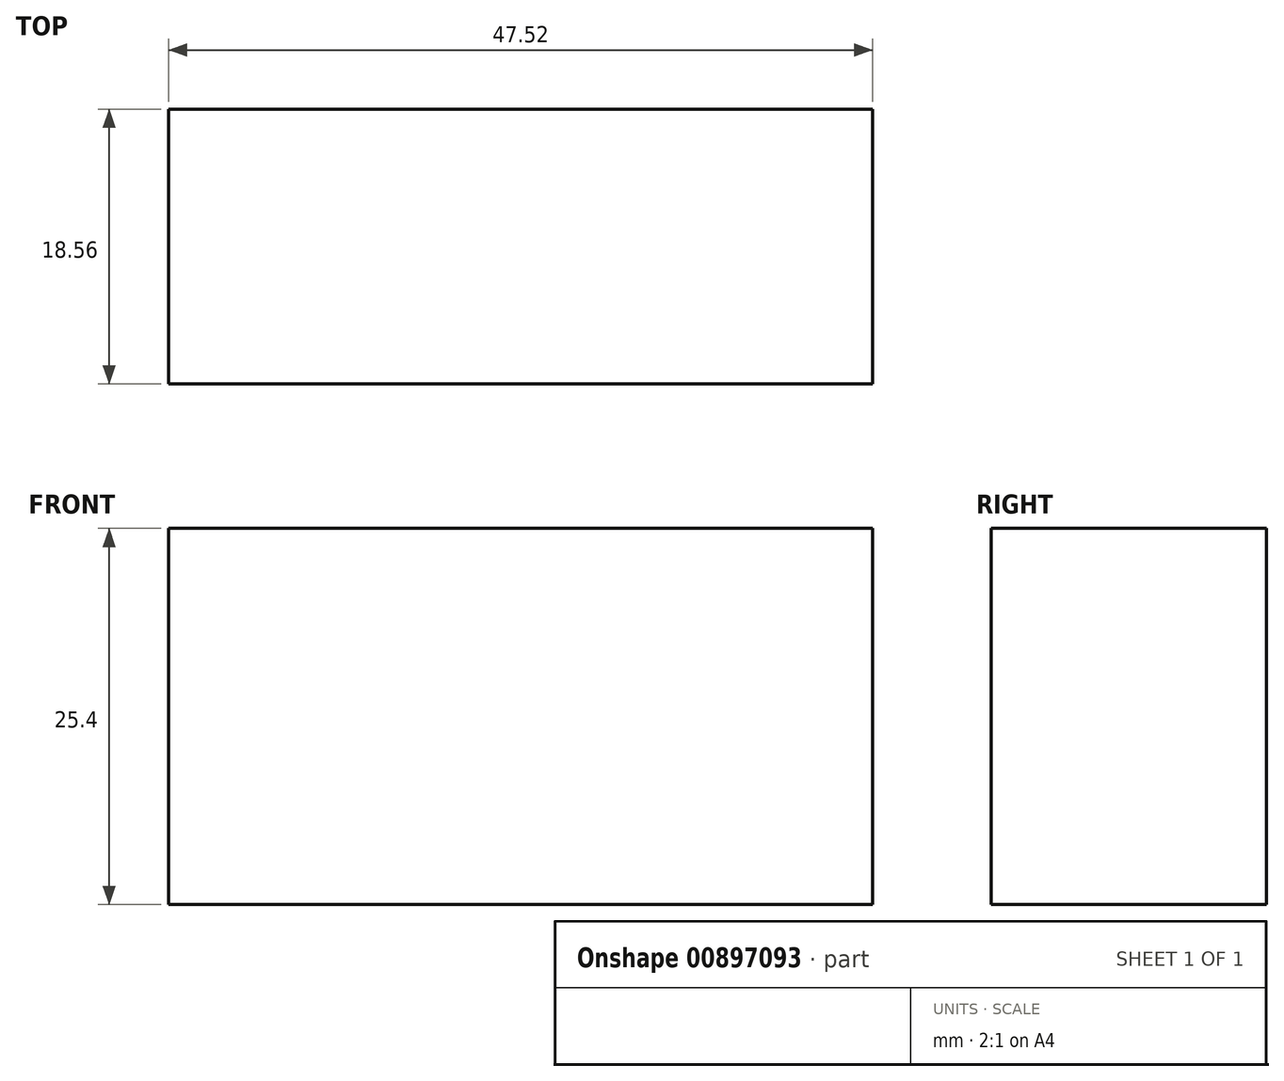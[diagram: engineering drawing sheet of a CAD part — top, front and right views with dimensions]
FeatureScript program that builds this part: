
annotation { "Feature Type Name" : "Feature", "Feature Type Description" : "" }
export const myFeature = defineFeature(function(context is Context, id is Id, definition is map)
    precondition{}
    {
        {
            var Q0;
            Q0=qCreatedBy(makeId("Top.planeOp"),FACE);
            var sketch = newSketch(context, id + "F0", { "sketchPlane" : qUnion([Q0])});
            skLineSegment(sketch, "E0.bottom", {"start": v(-55.48, 57.13) * mm, "end": v(-7.96, 57.13) * mm});
            skLineSegment(sketch, "E0.top", {"start": v(-55.48, 38.57) * mm, "end": v(-7.96, 38.57) * mm});
            skLineSegment(sketch, "E0.left", {"start": v(-55.48, 57.13) * mm, "end": v(-55.48, 38.57) * mm});
            skLineSegment(sketch, "E0.right", {"start": v(-7.96, 57.13) * mm, "end": v(-7.96, 38.57) * mm});
            skSolve(sketch);
        }
        {
            var Q0;
            Q0 = qSketchRegion(id + "F0", true);
            extrude(context, id + "F1", {"entities" : qUnion([Q0]), "depth" : 25.4 * mm, "offsetDistance" : 25.4 * mm});
        }
    });
